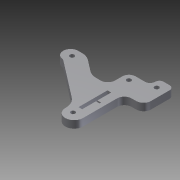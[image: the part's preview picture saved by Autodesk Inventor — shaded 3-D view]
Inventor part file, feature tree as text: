
AUTODESK INVENTOR PART (.ipt)
format: ipt  version: 2012 (Build 160160000, 160)  size: 157,696 bytes
history: native  units: mm
features: sketch x2, extrude x1, hole x1
ambient origin geometry x8: Origin, YZ Plane, XZ Plane, XY Plane, X Axis, Y Axis, Z Axis, Center Point
bodies: Solid1 (feature_tree)
feature tree (4):
  extrude  "Extrusion1"  Depth=5.0mm TaperAngle=0.0deg
  hole  "Hole1"  [1 undecoded]
  sketch  "Sketch1"  dims[d0=1.25mm d1=2.5mm d2=19.8mm d3=5.0mm d4=9.4mm d5=2.5mm d6=1.0mm d7=5.0mm d8=5.0mm d9=10.0mm d10=10.0mm d11=5.0mm d12=3.0mm d13=3.0mm d14=5.0mm d15=0.0mm]
  sketch  "Sketch2"  dims[d16=1.25mm d17=2.5mm d18=19.8mm d19=5.0mm d20=9.4mm d21=2.5mm d22=1.0mm d23=5.0mm d24=5.0mm d25=10.0mm d26=10.0mm d27=5.0mm d28=3.0mm d29=3.0mm d30=3.0mm d31=6.0mm d32=4.0mm d33=2.0mm d34=90.0deg d35=8.0mm d36=20.594885mm]
note: 1 required parameter value undecoded (feature->parameter linkage not recoverable at this tier; creation-order binding heuristic only, values carry confidence <= 0.55)
